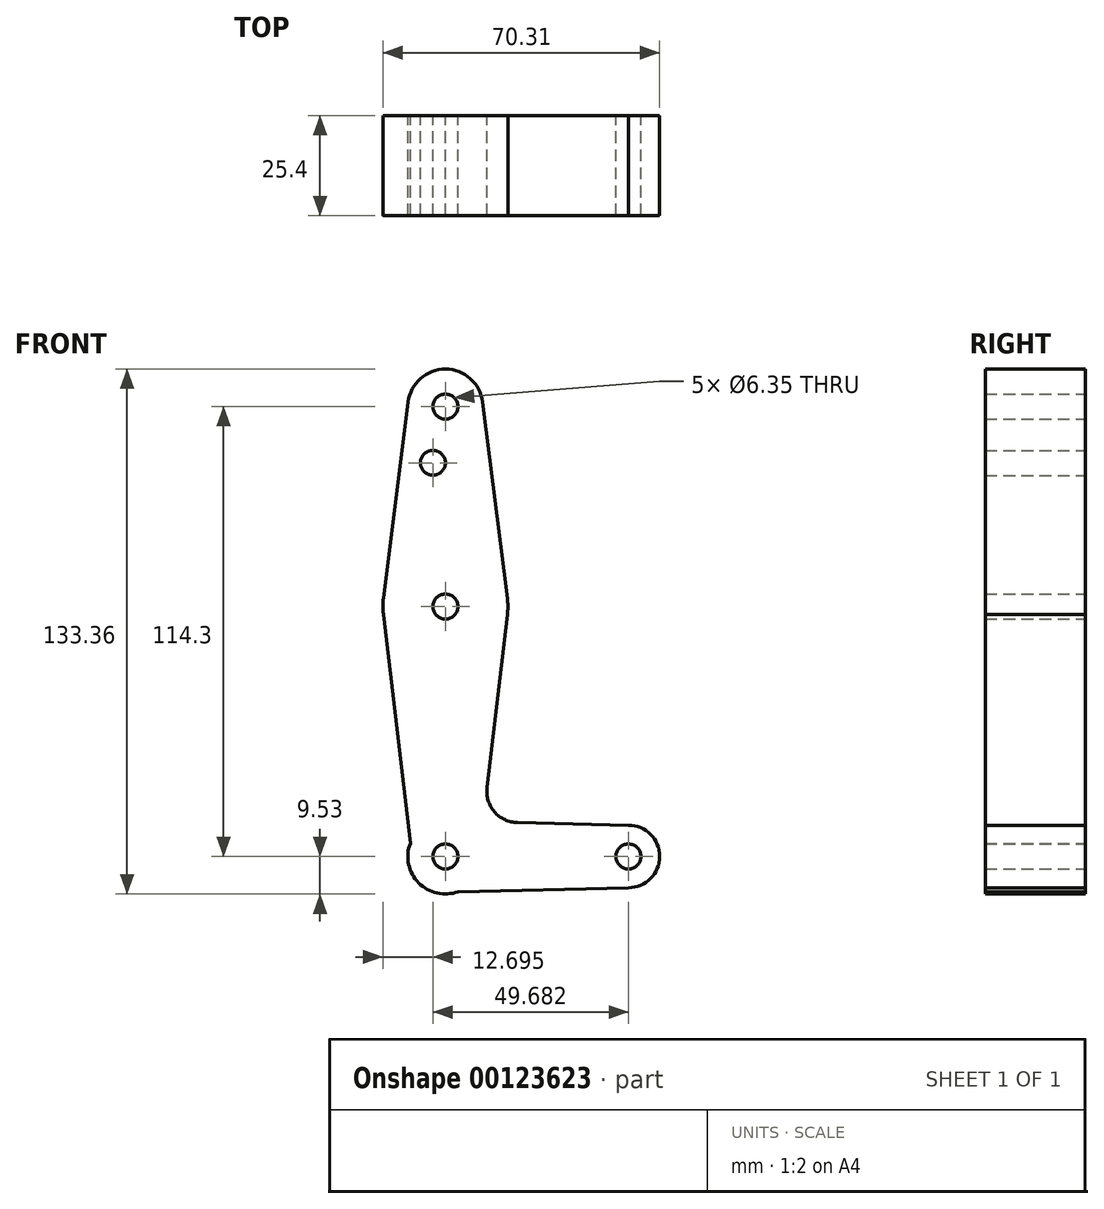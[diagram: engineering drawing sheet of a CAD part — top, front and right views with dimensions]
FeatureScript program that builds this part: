
annotation { "Feature Type Name" : "Feature", "Feature Type Description" : "" }
export const myFeature = defineFeature(function(context is Context, id is Id, definition is map)
    precondition{}
    {
        {
            var Q0;
            Q0=qCreatedBy(makeId("Front.planeOp"),FACE);
            var sketch = newSketch(context, id + "F0", { "sketchPlane" : qUnion([Q0])});
            skLineSegment(sketch, "E0", {"start": v(0, 0) * mm, "end": v(0, 114.3) * mm, "construction": true});
            skLineSegment(sketch, "E1", {"start": v(0, 0) * mm, "end": v(46.5, 0) * mm, "construction": true});
            skCircle(sketch, "E2", {"center": v(0, 114.3) * mm, "radius": 9.53 * mm});
            skCircle(sketch, "E3", {"center": v(0, 63.5) * mm, "radius": 15.88 * mm});
            skCircle(sketch, "E4", {"center": v(0, 0) * mm, "radius": 9.53 * mm});
            skCircle(sketch, "E5", {"center": v(46.5, 0) * mm, "radius": 7.94 * mm});
            skLineSegment(sketch, "E6", {"start": v(-9.46, 115.43) * mm, "end": v(-15.75, 65.48) * mm});
            skLineSegment(sketch, "E7", {"start": v(-15.74, 61.44) * mm, "end": v(-8.92, 3.35) * mm});
            skLineSegment(sketch, "E8", {"start": v(9.46, 115.43) * mm, "end": v(15.75, 65.48) * mm});
            skLineSegment(sketch, "E9", {"start": v(15.74, 61.44) * mm, "end": v(10.58, 17.48) * mm});
            skLineSegment(sketch, "E10", {"start": v(18.28, 8.6) * mm, "end": v(46.5, 7.94) * mm});
            skLineSegment(sketch, "E11", {"start": v(3.25, -8.96) * mm, "end": v(46.5, -7.94) * mm});
            skCircle(sketch, "E12", {"center": v(0, 114.3) * mm, "radius": 3.18 * mm});
            skCircle(sketch, "E13", {"center": v(-3.18, 100.03) * mm, "radius": 3.18 * mm});
            skCircle(sketch, "E14", {"center": v(0, 63.5) * mm, "radius": 3.18 * mm});
            skCircle(sketch, "E15", {"center": v(0, 0) * mm, "radius": 3.18 * mm});
            skCircle(sketch, "E16", {"center": v(46.5, 0) * mm, "radius": 3.18 * mm});
            skPoint(sketch, "E17.newPointA", {"position": v(8.92, 3.35) * mm});
            skPoint(sketch, "E17.newPointB", {"position": v(3.25, 8.96) * mm});
            skArc(sketch, "E17.filletArc", {"start": v(10.58, 17.48) * mm, "mid": v(12.47, 11.34) * mm, "end": v(18.28, 8.6) * mm});
            skSolve(sketch);
        }
        {
            var Q0;
            {var subQ0=sQuery(id+"F0.wireOp",EDGE,"E7");Q0=makeQuery(id+"F0.imprint","IMPRINT",FACE,{"disambiguationData":[TD([[makeQuery(id+"F0.imprint","IMPRINT",EDGE,{"derivedFrom":subQ0}),1.0]])]});}
            var Q1;
            Q1=makeQuery(id+"F0.imprint","IMPRINT",FACE,{"disambiguationData":[TD([[makeQuery(id+"F0.imprint","IMPRINT",EDGE,{"derivedFrom":sQuery(id+"F0.wireOp",EDGE,"E15")}),-1.0]])]});
            var Q2;
            Q2=makeQuery(id+"F0.imprint","IMPRINT",FACE,{"disambiguationData":[TD([[makeQuery(id+"F0.imprint","IMPRINT",EDGE,{"derivedFrom":sQuery(id+"F0.wireOp",EDGE,"E16")}),-1.0]])]});
            var Q3;
            Q3=makeQuery(id+"F0.imprint","IMPRINT",FACE,{"disambiguationData":[TD([[makeQuery(id+"F0.imprint","IMPRINT",EDGE,{"derivedFrom":sQuery(id+"F0.wireOp",EDGE,"E14")}),-1.0]])]});
            var Q4;
            {var subQ1=sQuery(id+"F0.wireOp",EDGE,"E6");Q4=makeQuery(id+"F0.imprint","IMPRINT",FACE,{"disambiguationData":[TD([[makeQuery(id+"F0.imprint","IMPRINT",EDGE,{"derivedFrom":subQ1}),1.0]])]});}
            var Q5;
            Q5=makeQuery(id+"F0.imprint","IMPRINT",FACE,{"disambiguationData":[TD([[makeQuery(id+"F0.imprint","IMPRINT",EDGE,{"derivedFrom":sQuery(id+"F0.wireOp",EDGE,"E12")}),-1.0]])]});
            extrude(context, id + "F1", {"entities" : qUnion([Q0, Q1, Q2, Q3, Q4, Q5]), "depth" : 25.4 * mm});
        }
    });
